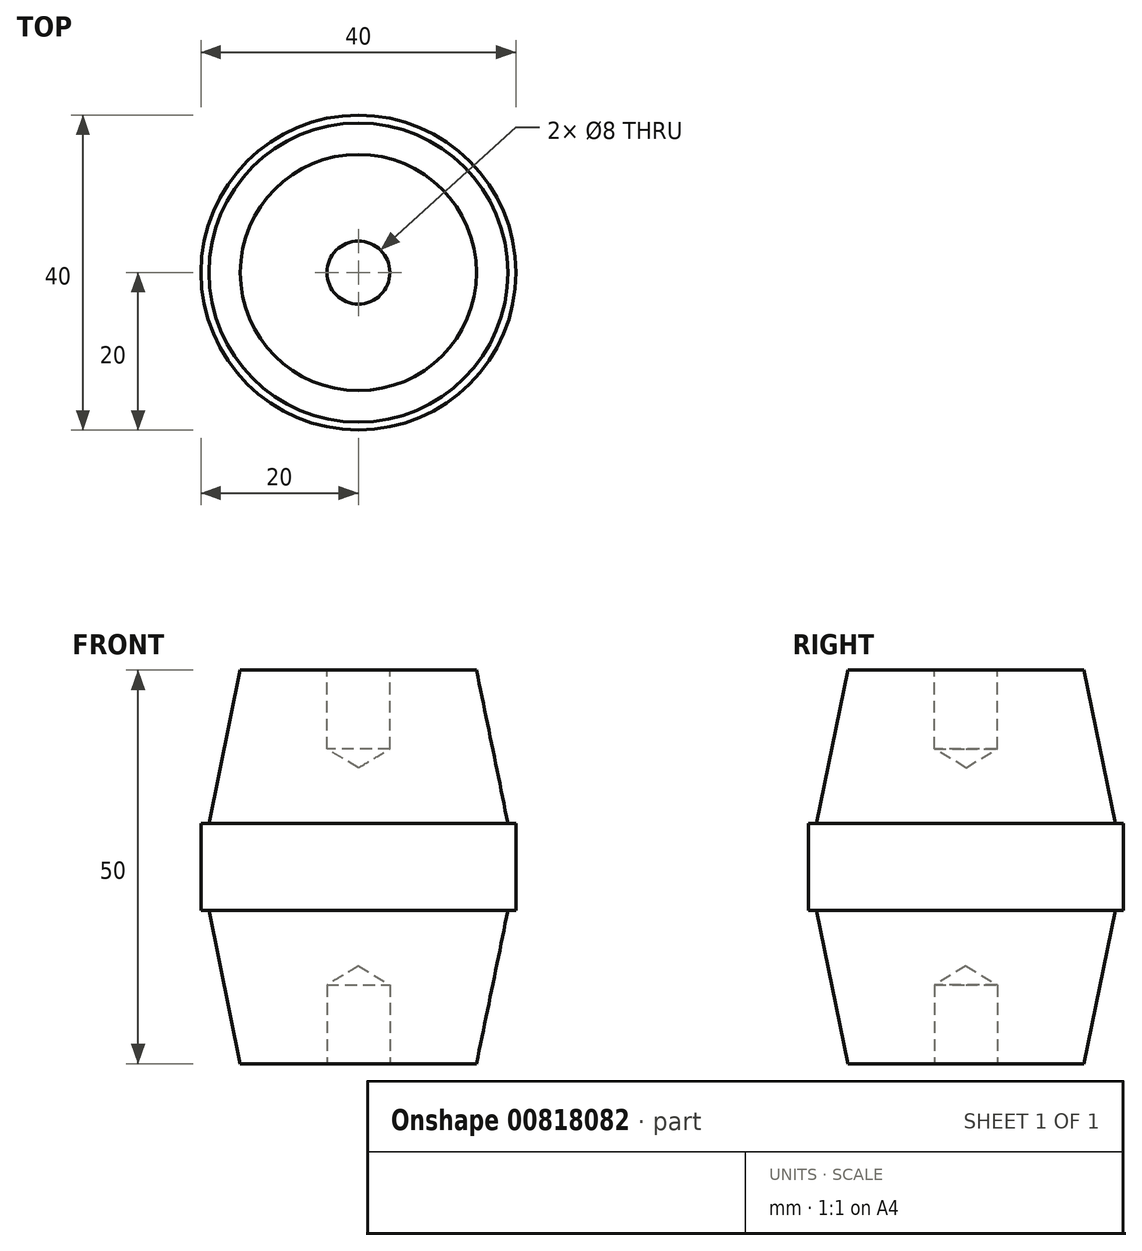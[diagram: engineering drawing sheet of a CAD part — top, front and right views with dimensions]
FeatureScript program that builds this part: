
annotation { "Feature Type Name" : "Feature", "Feature Type Description" : "" }
export const myFeature = defineFeature(function(context is Context, id is Id, definition is map)
    precondition{}
    {
        {
            var Q0;
            Q0=qCreatedBy(makeId("Front.planeOp"),FACE);
            var sketch = newSketch(context, id + "F0", { "sketchPlane" : qUnion([Q0])});
            skPoint(sketch, "E0.middle", {"position": v(0, 0) * mm});
            skLineSegment(sketch, "E1.0", {"start": v(0, 25) * mm, "end": v(-15, 25) * mm});
            skLineSegment(sketch, "E1.2", {"start": v(0, -25) * mm, "end": v(-15, -25) * mm});
            skLineSegment(sketch, "E1.3", {"start": v(-20, 5.5) * mm, "end": v(-20, -5.51) * mm});
            skLineSegment(sketch, "E2.left", {"start": v(0, 25) * mm, "end": v(0, -25) * mm});
            skLineSegment(sketch, "E3", {"start": v(-20, 0) * mm, "end": v(-20, 5.5) * mm});
            skLineSegment(sketch, "E4.MirrorCS", {"start": v(-20, 0) * mm, "end": v(-20, -5.5) * mm});
            skLineSegment(sketch, "E5.bottom", {"start": v(-20, 5.5) * mm, "end": v(-19, 5.5) * mm});
            skLineSegment(sketch, "E5.top", {"start": v(-20, -5.51) * mm, "end": v(-19, -5.51) * mm});
            skLineSegment(sketch, "E6", {"start": v(-19, 5.5) * mm, "end": v(-15, 25) * mm});
            skLineSegment(sketch, "E7", {"start": v(-19, -5.51) * mm, "end": v(-15, -25) * mm});
            skSolve(sketch);
        }
        {
            var Q0;
            Q0=makeQuery(id+"F0.imprint","IMPRINT",FACE,{"disambiguationData":[TD([[makeQuery(id+"F0.imprint","IMPRINT",EDGE,{"derivedFrom":sQuery(id+"F0.wireOp",EDGE,"E1.0")}),1.0]])]});
            var Q1;
            Q1=sQuery(id+"F0.wireOp",EDGE,"E2.left");
            revolve(context, id + "F1", {"entities" : qUnion([Q0]), "axis" : qUnion([Q1]), "revolveType" : RevolveType.FULL});
        }
        {
            var Q0;
            Q0=makeQuery(id+"F1.opRevolve","SWEPT_FACE",FACE,{"disambiguationData":[OSD([sQuery(id+"F0.wireOp",EDGE,"E1.0")])]});
            var sketch = newSketch(context, id + "F2", { "sketchPlane" : qUnion([Q0])});
            skPoint(sketch, "E8", {"position": v(0, 0) * mm});
            skSolve(sketch);
        }
        {
            var Q0;
            Q0=makeQuery(id+"F1.opRevolve","SWEPT_FACE",FACE,{"disambiguationData":[OSD([sQuery(id+"F0.wireOp",EDGE,"E1.2")])]});
            var sketch = newSketch(context, id + "F3", { "sketchPlane" : qUnion([Q0])});
            skPoint(sketch, "E9", {"position": v(0, 0) * mm});
            skSolve(sketch);
        }
        {
            var Q0;
            Q0=sQuery(id+"F3.wireOp",VERTEX,"E9");
            var Q1;
            Q1=sQuery(id+"F2.wireOp",VERTEX,"E8");
            var Q2;
            Q2=makeQuery(id+"F1.opRevolve","SWEPT_BODY",BODY,{"disambiguationData":[OSD([sQuery(id+"F0.wireOp",EDGE,"E1.0"),sQuery(id+"F0.wireOp",EDGE,"E1.2"),sQuery(id+"F0.wireOp",EDGE,"E1.3"),sQuery(id+"F0.wireOp",EDGE,"mtK3qn9K-haMW-uVY2-Y3Av-eEPCaIJVO75R.bottom"),sQuery(id+"F0.wireOp",EDGE,"mtK3qn9K-haMW-uVY2-Y3Av-eEPCaIJVO75R.left"),sQuery(id+"F0.wireOp",EDGE,"558dGJd4-tOWL-0JkX-FYeg-ERiVoFfM81lT.bottom"),sQuery(id+"F0.wireOp",EDGE,"558dGJd4-tOWL-0JkX-FYeg-ERiVoFfM81lT.left"),sQuery(id+"F0.wireOp",EDGE,"E2.left")])]});
            hole(context, id + "F4", {"style" : HoleStyle.SIMPLE, "endStyle" : HoleEndStyle.BLIND, "holeDiameter" : 8 * mm, "holeDepth" : 10 * mm, "locations" : qUnion([Q0, Q1]), "scope" : qUnion([Q2]), "majorDiameter" : 5 * mm, "tappedDepth" : 12 * mm, "tapClearance" : 3});
        }
    });
